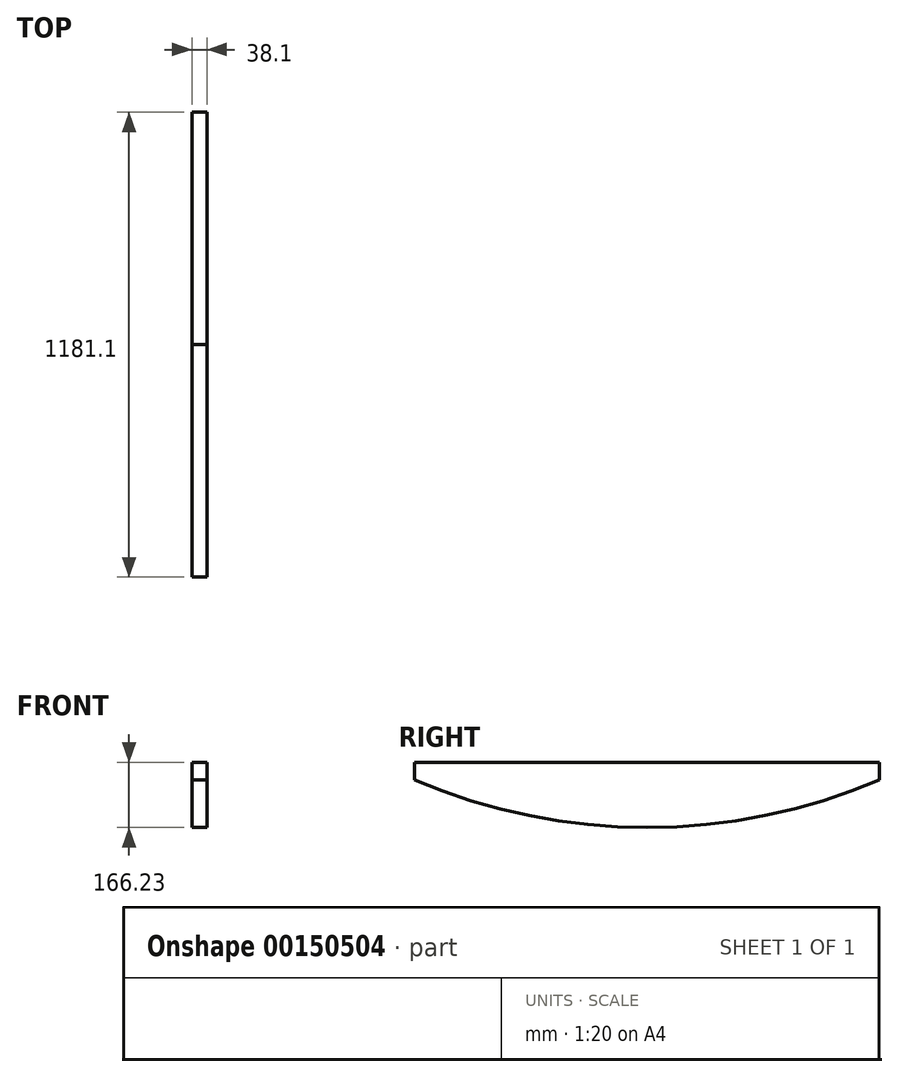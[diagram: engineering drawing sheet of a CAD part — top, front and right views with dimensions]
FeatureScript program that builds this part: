
annotation { "Feature Type Name" : "Feature", "Feature Type Description" : "" }
export const myFeature = defineFeature(function(context is Context, id is Id, definition is map)
    precondition{}
    {
        {
            var Q0;
            Q0=qCreatedBy(makeId("Right.planeOp"),FACE);
            var sketch = newSketch(context, id + "F2", { "sketchPlane" : qUnion([Q0])});
            skLineSegment(sketch, "E0", {"start": v(-590.55, 0) * mm, "end": v(590.55, 0) * mm});
            skLineSegment(sketch, "E1", {"start": v(590.55, 0) * mm, "end": v(590.55, -44.45) * mm});
            skLineSegment(sketch, "E2", {"start": v(-590.55, 0) * mm, "end": v(-590.55, -44.45) * mm});
            skArc(sketch, "E3", {"start": v(-590.55, -44.45) * mm, "mid": v(0, -166.23) * mm, "end": v(590.55, -44.45) * mm});
            skLineSegment(sketch, "E4", {"start": v(0, 0) * mm, "end": v(0, 0) * mm});
            skLineSegment(sketch, "E5", {"start": v(1.02, -0.3) * mm, "end": v(0, 0) * mm});
            skLineSegment(sketch, "E6", {"start": v(0.01, -155.66) * mm, "end": v(0.01, 7.71) * mm});
            skSolve(sketch);
        }
        {
            var Q0;
            Q0=makeQuery(id+"F2.imprint","IMPRINT",FACE,{"disambiguationData":[TD([[makeQuery(id+"F2.imprint","IMPRINT",EDGE,{"derivedFrom":sQuery(id+"F2.wireOp",EDGE,"E0")}),-1.0]])]});
            extrude(context, id + "F0", {"entities" : qUnion([Q0]), "depth" : 38.1 * mm});
        }
    });
